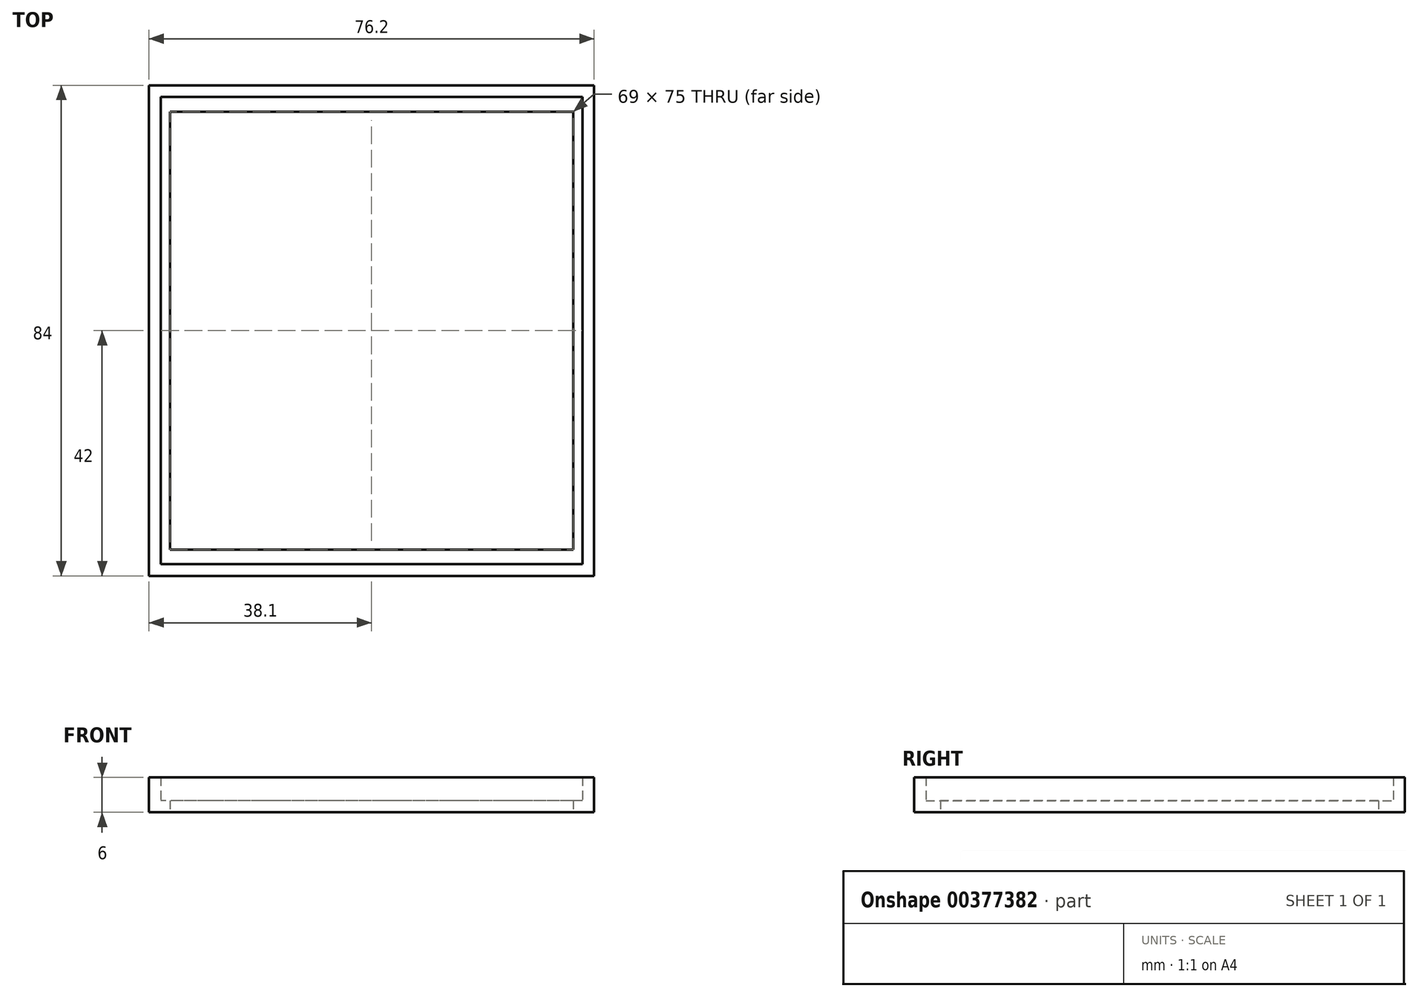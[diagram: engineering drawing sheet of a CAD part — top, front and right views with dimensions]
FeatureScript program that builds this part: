
annotation { "Feature Type Name" : "Feature", "Feature Type Description" : "" }
export const myFeature = defineFeature(function(context is Context, id is Id, definition is map)
    precondition{}
    {
        {
            var Q0;
            Q0=qCreatedBy(makeId("Top.planeOp"),FACE);
            var sketch = newSketch(context, id + "F0", { "sketchPlane" : qUnion([Q0])});
            skLineSegment(sketch, "E0.bottom", {"start": v(34.5, 37.5) * mm, "end": v(-34.5, 37.5) * mm});
            skLineSegment(sketch, "E0.top", {"start": v(34.5, -37.5) * mm, "end": v(-34.5, -37.5) * mm});
            skLineSegment(sketch, "E0.left", {"start": v(34.5, 37.5) * mm, "end": v(34.5, -37.5) * mm});
            skLineSegment(sketch, "E0.right", {"start": v(-34.5, 37.5) * mm, "end": v(-34.5, -37.5) * mm});
            skPoint(sketch, "E0.middle", {"position": v(0, 0) * mm});
            skLineSegment(sketch, "E1.bottom", {"start": v(36.1, -40) * mm, "end": v(-36.1, -40) * mm});
            skLineSegment(sketch, "E1.top", {"start": v(36.1, 40) * mm, "end": v(-36.1, 40) * mm});
            skLineSegment(sketch, "E1.left", {"start": v(36.1, -40) * mm, "end": v(36.1, 40) * mm});
            skLineSegment(sketch, "E1.right", {"start": v(-36.1, -40) * mm, "end": v(-36.1, 40) * mm});
            skLineSegment(sketch, "E2.0", {"start": v(-38.1, -42) * mm, "end": v(-38.1, 42) * mm});
            skLineSegment(sketch, "E2.1", {"start": v(38.1, -42) * mm, "end": v(-38.1, -42) * mm});
            skLineSegment(sketch, "E2.2", {"start": v(38.1, -42) * mm, "end": v(38.1, 42) * mm});
            skLineSegment(sketch, "E2.3", {"start": v(38.1, 42) * mm, "end": v(-38.1, 42) * mm});
            skSolve(sketch);
        }
        {
            var Q0;
            Q0=makeQuery(id+"F0.imprint","IMPRINT",FACE,{"disambiguationData":[TD([[makeQuery(id+"F0.imprint","IMPRINT",EDGE,{"derivedFrom":sQuery(id+"F0.wireOp",EDGE,"E0.bottom")}),-1.0]])]});
            extrude(context, id + "F1", {"entities" : qUnion([Q0]), "depth" : 2 * mm});
        }
        {
            var Q0;
            Q0=makeQuery(id+"F0.imprint","IMPRINT",FACE,{"disambiguationData":[TD([[makeQuery(id+"F0.imprint","IMPRINT",EDGE,{"derivedFrom":sQuery(id+"F0.wireOp",EDGE,"E1.bottom")}),1.0]])]});
            extrude(context, id + "F2", {"entities" : qUnion([Q0]), "operationType" : NewBodyOperationType.ADD, "depth" : (2 + 4) * mm});
        }
    });
